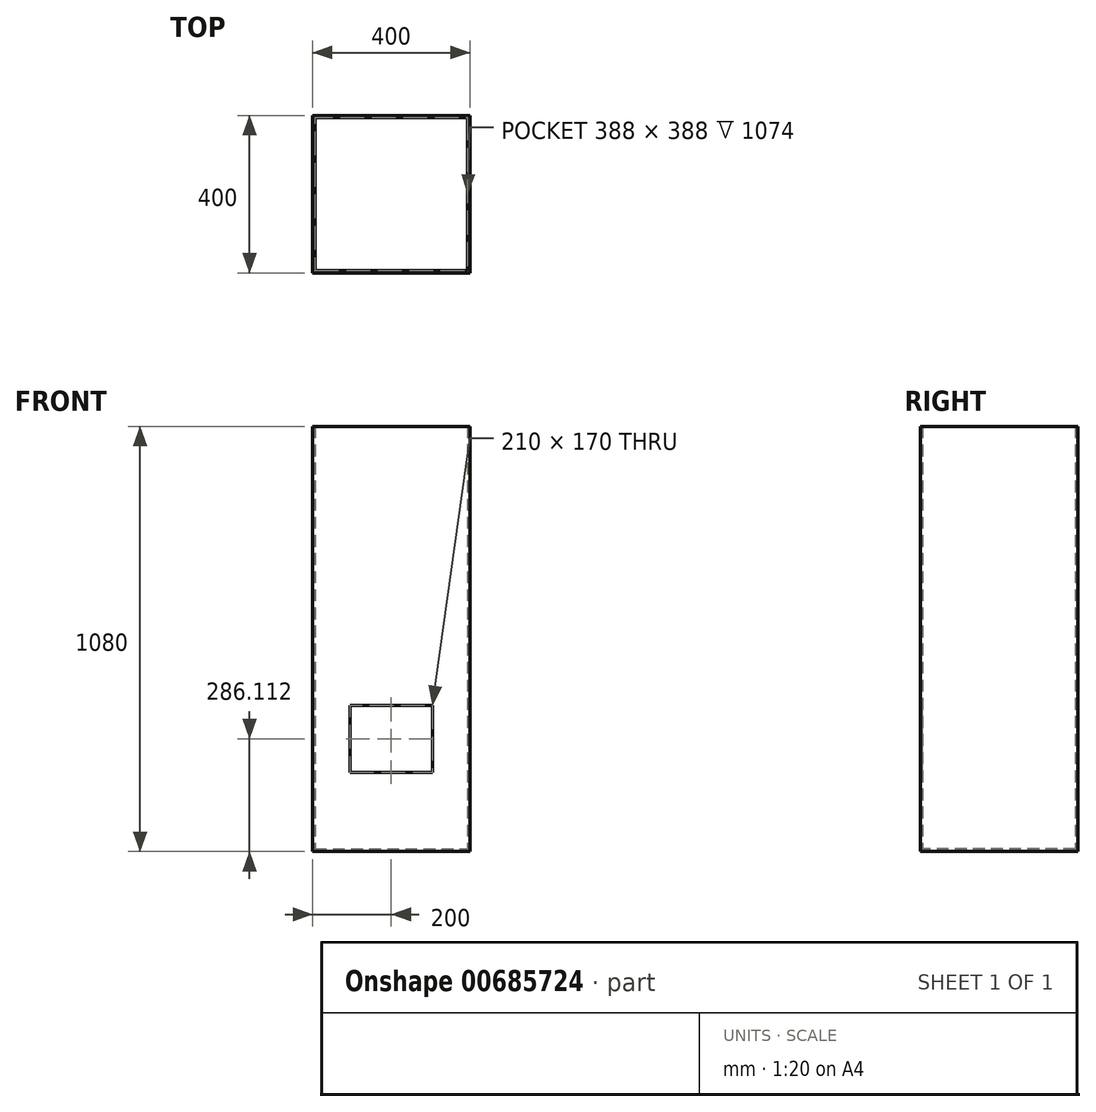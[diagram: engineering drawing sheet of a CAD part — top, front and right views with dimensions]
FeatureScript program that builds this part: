
annotation { "Feature Type Name" : "Feature", "Feature Type Description" : "" }
export const myFeature = defineFeature(function(context is Context, id is Id, definition is map)
    precondition{}
    {
        {
            var Q0;
            Q0=qCreatedBy(makeId("Top.planeOp"),FACE);
            var sketch = newSketch(context, id + "F0", { "sketchPlane" : qUnion([Q0])});
            skLineSegment(sketch, "E0.bottom", {"start": v(200, 200) * mm, "end": v(-200, 200) * mm});
            skLineSegment(sketch, "E0.top", {"start": v(200, -200) * mm, "end": v(-200, -200) * mm});
            skLineSegment(sketch, "E0.left", {"start": v(200, 200) * mm, "end": v(200, -200) * mm});
            skLineSegment(sketch, "E0.right", {"start": v(-200, 200) * mm, "end": v(-200, -200) * mm});
            skPoint(sketch, "E0.middle", {"position": v(0, 0) * mm});
            skLineSegment(sketch, "E1.bottom", {"start": v(-194, 194) * mm, "end": v(194, 194) * mm});
            skLineSegment(sketch, "E1.top", {"start": v(-194, -194) * mm, "end": v(194, -194) * mm});
            skLineSegment(sketch, "E1.left", {"start": v(-194, 194) * mm, "end": v(-194, -194) * mm});
            skLineSegment(sketch, "E1.right", {"start": v(194, 194) * mm, "end": v(194, -194) * mm});
            skSolve(sketch);
        }
        {
            var Q0;
            Q0=makeQuery(id+"F0.imprint","IMPRINT",FACE,{"disambiguationData":[TD([[makeQuery(id+"F0.imprint","IMPRINT",EDGE,{"derivedFrom":sQuery(id+"F0.wireOp",EDGE,"E1.bottom")}),-1.0]])]});
            extrude(context, id + "F1", {"entities" : qUnion([Q0]), "depth" : 6 * mm, "offsetDistance" : 25 * mm});
        }
        {
            var Q0;
            Q0=makeQuery(id+"F0.imprint","IMPRINT",FACE,{"disambiguationData":[TD([[makeQuery(id+"F0.imprint","IMPRINT",EDGE,{"derivedFrom":sQuery(id+"F0.wireOp",EDGE,"E0.bottom")}),1.0]])]});
            extrude(context, id + "F2", {"entities" : qUnion([Q0]), "operationType" : NewBodyOperationType.ADD, "depth" : 1080 * mm, "offsetDistance" : 25 * mm});
        }
        {
            var Q0;
            Q0=makeQuery(id+"F2.opExtrude","SWEPT_FACE",FACE,{"disambiguationData":[OSD([sQuery(id+"F0.wireOp",EDGE,"E0.top")])]});
            var sketch = newSketch(context, id + "F3", { "sketchPlane" : qUnion([Q0])});
            skLineSegment(sketch, "E2.bottom", {"start": v(-105, 371.11) * mm, "end": v(105, 371.11) * mm});
            skLineSegment(sketch, "E2.top", {"start": v(-105, 201.11) * mm, "end": v(105, 201.11) * mm});
            skLineSegment(sketch, "E2.left", {"start": v(-105, 371.11) * mm, "end": v(-105, 201.11) * mm});
            skLineSegment(sketch, "E2.right", {"start": v(105, 371.11) * mm, "end": v(105, 201.11) * mm});
            skPoint(sketch, "E2.middle", {"position": v(0, 286.11) * mm});
            skPoint(sketch, "E2.middle.positionSnap0", {"position": v(0, 0) * mm});
            skPoint(sketch, "E2.centerSnap0", {"position": v(0, 0) * mm});
            skSolve(sketch);
        }
        {
            var Q0;
            Q0=makeQuery(id+"F3.imprint","IMPRINT",FACE,{"disambiguationData":[TD([[makeQuery(id+"F3.imprint","IMPRINT",EDGE,{"derivedFrom":sQuery(id+"F3.wireOp",EDGE,"E2.bottom")}),-1.0]])]});
            extrude(context, id + "F4", {"entities" : qUnion([Q0]), "operationType" : NewBodyOperationType.REMOVE, "oppositeDirection" : true, "depth" : 25 * mm, "offsetDistance" : 25 * mm});
        }
    });
